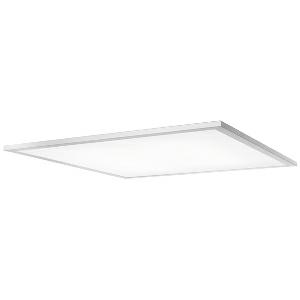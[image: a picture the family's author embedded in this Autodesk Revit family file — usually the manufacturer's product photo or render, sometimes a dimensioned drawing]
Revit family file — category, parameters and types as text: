
# Revit family: dotoo_fit_-_dfe_4000_830_sm600_00808121_2aa2
name_source: partatom
category: Lighting Fixtures
units: mm (PartAtom-declared; Revit-internal decimal feet)

## family parameters
Cut with Voids When Loaded = No
Host = Face
Light Source = No
Part Type = Normal
Room Calculation Point = No
Round Connector Dimension = Use Diameter
Shared = No

## types (1)
- DOTOO.fit - DFE 4000/830 SM600 (1 x LED, 3900 lm, 4000K)
    Apparent Load = 30 VA
    Approval mark = CE
    CIE Flux Codes = 66 90 98 100 100
    Color Rendering = 80-89
    Color Temperature = 4000K
    Control Gear = Electronic ballast
    Default Elevation = 1800 mm
    Description = DFE 4000/830|Recessed modular luminaire|light source:  |work equipment: Electronic ballast|connected load: 220-240 V, 50/60 Hz|Power consumption: approx. 30 W|standby: approx. 0,50|power factor: approx. 0,900|luminous flux: 3900 lm|luminous efficacy: 130 lm/W|light distribution: Direct|direct ratio: approx. 100 %|colour temperature: Warm white, ca. 3000 K|color rendering index (CRI): >= 80|chromaticity tolerance:  3 SDCM|System of protection: IP 20|class of protection: II|technology: Switchable|operation: External|luminaire body|material: Sectional aluminium|colour: White|weight (net): approx. 2.9 kg|mains lead: 0.50 m Connector|glare control: Prism aperture|luminance(L65): <= 2600 cd/m|unified glare rating(4H 8H): <=  19|special features: Direct light component with edge light and light-guide technology for homogenous light exit, Flicker-free, System dimension 600 x 600 mm, Strain relief with the possibility of through-wiring|
    Height = 0 mm  [stored 0 ft]
    Lamp = 1 x LED
    Lamp Light Flux = 3900 lm
    Lamp count = 1
    Length = 596 mm
    Luminous efficacy = 130 lm/W
    Manufacturer = Waldmann
    ModVariant = No
    Model = 00808121
    Mounting Place = Ceiling
    Mounting Type = Recessed
    Number of Poles = 1
    OnlyDefault = Yes
    Power Factor = 1
    Product Name = DOTOO.fit - DFE 4000/830 SM600
    Product group = Recessed luminaire
    ProductGroupID = 4
    Protection Class = Protection class II
    Protection Degree = IP 20
    RLX_Detail_Level = 1
    RLX_Emergency_Light_Flux = 0 lm
    RLX_Emergency_Type = 0
    RLX_Emergency_Type_DB = No
    RlxData = <blob elided: 37353 chars, md5=99ac2817>
    Socket = socket
    Standby Power = 0 W
    System Light Flux = 3900 lm
    System Power = 30 W
    Type Comments = Product without accessories
    Type Image = 113328000-00692486.jpg
    URL = http://relux.com
    VarID = ---
    Voltage = 230 V
    Voltage Range = 220-240 V
    Weight = 0.00 kg
    Width = 596 mm

note: [stored X ft] marks values corroborated as IEEE doubles in the binary element streams (Revit-internal decimal feet)

## geometry (parser evidence)
native form markers: Blend x4, Sweep x11
no freeform markers — native parametric forms only
